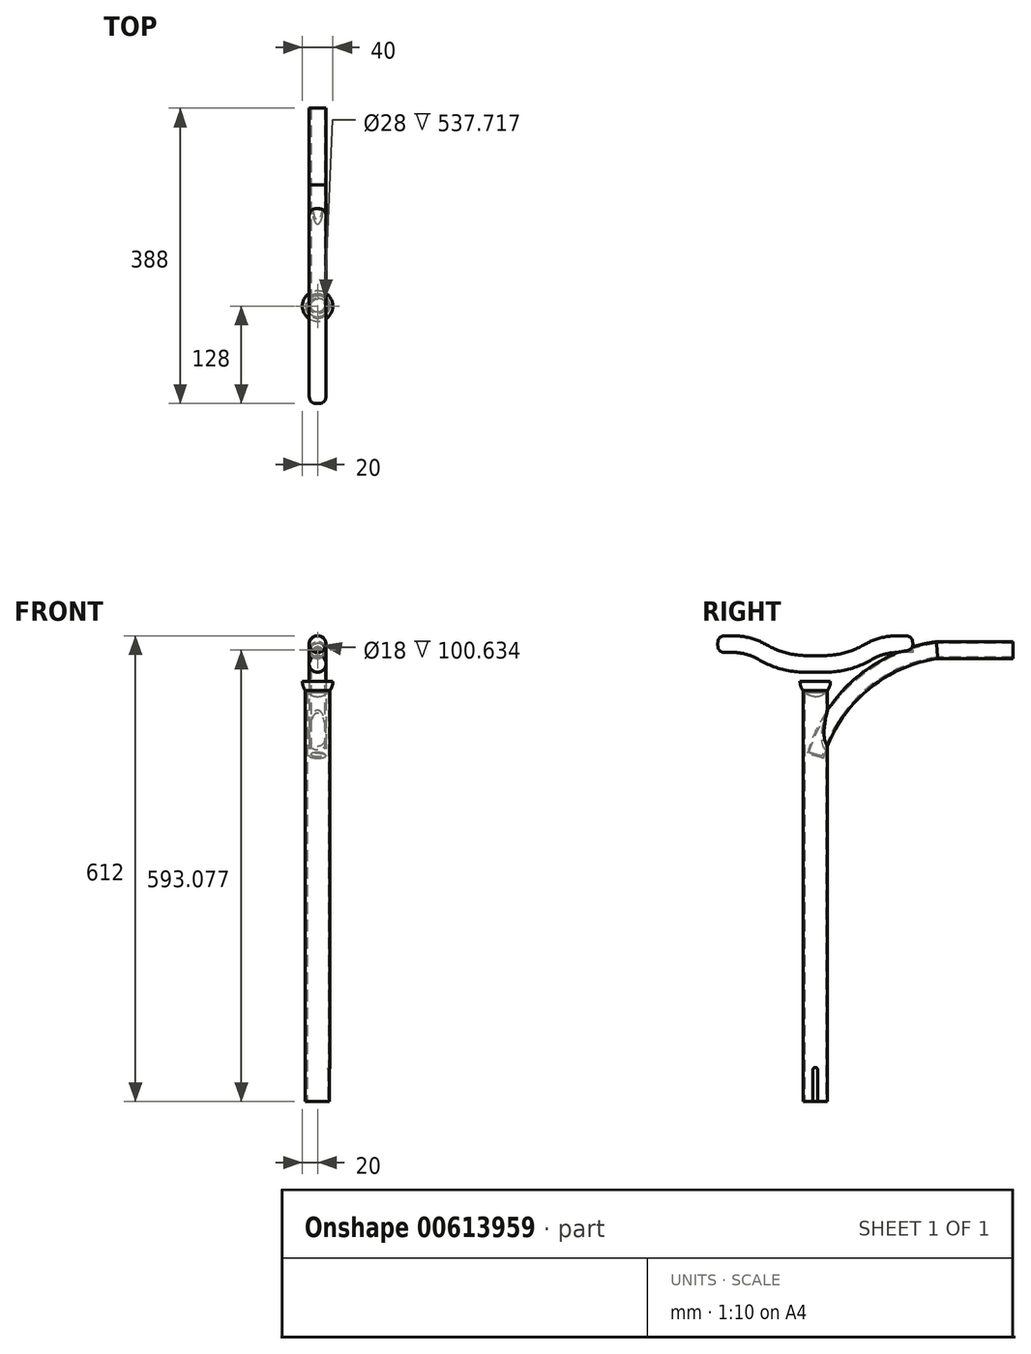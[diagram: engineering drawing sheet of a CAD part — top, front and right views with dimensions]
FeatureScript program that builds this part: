
annotation { "Feature Type Name" : "Feature", "Feature Type Description" : "" }
export const myFeature = defineFeature(function(context is Context, id is Id, definition is map)
    precondition{}
    {
        {
            var Q0;
            Q0=qCreatedBy(makeId("Top.planeOp"),FACE);
            var sketch = newSketch(context, id + "F0", { "sketchPlane" : qUnion([Q0])});
            skCircle(sketch, "E0", {"center": v(0, 0) * mm, "radius": 16 * mm});
            skSolve(sketch);
        }
        {
            var Q0;
            Q0 = qSketchRegion(id + "F0", true);
            extrude(context, id + "F1", {"entities" : qUnion([Q0]), "depth" : 550 * mm, "offsetDistance" : 25 * mm});
        }
        {
            var Q0;
            Q0=makeQuery(id+"F1.opExtrude","CAP_FACE",FACE,{"disambiguationData":[OSD([sQuery(id+"F0.wireOp",EDGE,"E0")])],"isStart":true});
            shell(context, id + "F2", {"entities" : qUnion([Q0]), "thickness" : 2 * mm});
        }
        {
            var Q0;
            Q0=qCreatedBy(makeId("Right.planeOp"),FACE);
            var sketch = newSketch(context, id + "F3", { "sketchPlane" : qUnion([Q0])});
            skLineSegment(sketch, "E1.bottom", {"start": v(-3, 0) * mm, "end": v(3, 0) * mm});
            skLineSegment(sketch, "E1.top", {"start": v(0, 45) * mm, "end": v(0, 45) * mm});
            skLineSegment(sketch, "E1.left", {"start": v(-3, 0) * mm, "end": v(-3, 42) * mm});
            skLineSegment(sketch, "E1.right", {"start": v(3, 0) * mm, "end": v(3, 42) * mm});
            skPoint(sketch, "E2.visualSharp", {"position": v(-3, 45) * mm});
            skArc(sketch, "E2.filletArc", {"start": v(0, 45) * mm, "mid": v(-2.12, 44.12) * mm, "end": v(-3, 42) * mm});
            skPoint(sketch, "E3.visualSharp", {"position": v(3, 45) * mm});
            skArc(sketch, "E3.filletArc", {"start": v(3, 42) * mm, "mid": v(2.12, 44.12) * mm, "end": v(0, 45) * mm});
            skSolve(sketch);
        }
        {
            var Q0;
            Q0 = qSketchRegion(id + "F3", true);
            extrude(context, id + "F4", {"entities" : qUnion([Q0]), "operationType" : NewBodyOperationType.REMOVE, "endBound" : BoundingType.THROUGH_ALL, "depth" : 25 * mm, "offsetDistance" : 25 * mm});
        }
        {
            var Q0;
            Q0=qCreatedBy(makeId("Right.planeOp"),FACE);
            var sketch = newSketch(context, id + "F5", { "sketchPlane" : qUnion([Q0])});
            skArc(sketch, "E4", {"start": v(160, 593.08) * mm, "mid": v(59.5, 547.27) * mm, "end": v(0, 454.2) * mm});
            skLineSegment(sketch, "E5", {"start": v(160, 593.08) * mm, "end": v(260, 593.08) * mm});
            skSolve(sketch);
        }
        {
            var Q0;
            Q0=sQuery(id+"F5.wireOp",VERTEX,"E5.end");
            var Q1;
            Q1=qCreatedBy(makeId("Front.planeOp"),FACE);
            cPlane(context, id + "F6", {"entities" : qUnion([Q0, Q1]), "cplaneType" : CPlaneType.PLANE_POINT, "offset" : 25 * mm, "width" : 150 * mm, "height" : 150 * mm});
        }
        {
            var Q0;
            Q0=qCreatedBy(id+"F6.planeOp",FACE);
            var sketch = newSketch(context, id + "F7", { "sketchPlane" : qUnion([Q0])});
            skCircle(sketch, "E6", {"center": v(0, 593.08) * mm, "radius": 11 * mm});
            skSolve(sketch);
        }
        {
            var Q0;
            Q0=makeQuery(id+"F7.imprint","IMPRINT",FACE,{"disambiguationData":[TD([[makeQuery(id+"F7.imprint","IMPRINT",EDGE,{"derivedFrom":sQuery(id+"F7.wireOp",EDGE,"E6")}),1.0]])]});
            var Q1;
            Q1=sQuery(id+"F5.wireOp",EDGE,"E4");
            var Q2;
            Q2=sQuery(id+"F5.wireOp",EDGE,"E5");
            sweep(context, id + "F8", {"operationType" : NewBodyOperationType.ADD, "profiles" : qUnion([Q0]), "path" : qUnion([Q1, Q2])});
        }
        {
            var Q0;
            Q0=makeQuery(id+"F8.opSweep","CAP_FACE",FACE,{"disambiguationData":[OSD([sQuery(id+"F5.wireOp",VERTEX,"E5.end"),sQuery(id+"F7.wireOp",EDGE,"E6")])],"isStart":true});
            shell(context, id + "F9", {"entities" : qUnion([Q0]), "thickness" : 2 * mm});
        }
        {
            var Q0;
            Q0=qCreatedBy(makeId("Right.planeOp"),FACE);
            var sketch = newSketch(context, id + "F10", { "sketchPlane" : qUnion([Q0])});
            skLineSegment(sketch, "E7", {"start": v(0, 356.72) * mm, "end": v(0, 575) * mm, "construction": true});
            skLineSegment(sketch, "E8", {"start": v(-128, 601) * mm, "end": v(-108, 601) * mm});
            skArc(sketch, "E9", {"start": v(-69.28, 590.46) * mm, "mid": v(-87.93, 598.32) * mm, "end": v(-108, 601) * mm});
            skLineSegment(sketch, "E10", {"start": v(0, 575) * mm, "end": v(-12.5, 575) * mm});
            skArc(sketch, "E11", {"start": v(-69.28, 590.46) * mm, "mid": v(-41.92, 578.93) * mm, "end": v(-12.5, 575) * mm});
            skLineSegment(sketch, "E12.MirrorCS", {"start": v(0, 575) * mm, "end": v(12.5, 575) * mm});
            skArc(sketch, "E13.MirrorCS", {"start": v(69.28, 590.46) * mm, "mid": v(41.92, 578.93) * mm, "end": v(12.5, 575) * mm});
            skArc(sketch, "E14.MirrorCS", {"start": v(69.28, 590.46) * mm, "mid": v(87.93, 598.32) * mm, "end": v(108, 601) * mm});
            skLineSegment(sketch, "E15.MirrorCS", {"start": v(128, 601) * mm, "end": v(108, 601) * mm});
            skSolve(sketch);
        }
        {
            var Q0;
            Q0=sQuery(id+"F10.wireOp",VERTEX,"E15.MirrorCS.start");
            var Q1;
            Q1=qCreatedBy(id+"F6.planeOp",FACE);
            cPlane(context, id + "F11", {"entities" : qUnion([Q0, Q1]), "cplaneType" : CPlaneType.PLANE_POINT, "offset" : 25 * mm, "width" : 150 * mm, "height" : 150 * mm});
        }
        {
            var Q0;
            Q0=qCreatedBy(id+"F11.planeOp",FACE);
            var sketch = newSketch(context, id + "F12", { "sketchPlane" : qUnion([Q0])});
            skCircle(sketch, "E16", {"center": v(0, 601) * mm, "radius": 11 * mm});
            skSolve(sketch);
        }
        {
            var Q0;
            Q0 = qSketchRegion(id + "F12", true);
            var Q1;
            Q1 = qConstructionFilter(qBodyType(qCreatedBy(id + "F10" ,EDGE), BodyType.WIRE), ConstructionObject.NO);
            sweep(context, id + "F13", {"operationType" : NewBodyOperationType.ADD, "profiles" : qUnion([Q0]), "path" : qUnion([Q1])});
        }
        {
            var Q0;
            Q0=makeQuery(id+"F13.opSweep","CAP_EDGE",EDGE,{"disambiguationData":[OSD([sQuery(id+"F10.wireOp",VERTEX,"E8.start"),sQuery(id+"F12.wireOp",EDGE,"E16")])],"isStart":false});
            var Q1;
            {var subQ0=sQuery(id+"F12.wireOp",EDGE,"E16");var subQ1=sQuery(id+"F10.wireOp",VERTEX,"E15.MirrorCS.start");Q1=makeQuery(id+"F13.boolean.opBoolean","SPLIT",EDGE,{"disambiguationData":[TD([makeQuery(id+"F8.opSweep","SWEPT_FACE",FACE,{"disambiguationData":[OSD([sQuery(id+"F5.wireOp",EDGE,"E4"),sQuery(id+"F7.wireOp",EDGE,"E6")])]})])],"derivedFrom":makeQuery(id+"F13.opSweep","CAP_EDGE",EDGE,{"disambiguationData":[OSD([subQ1,subQ0])],"isStart":true})});}
            fillet(context, id + "F14", {"entities" : qUnion([Q0, Q1]), "radius" : 10 * mm, "tangentPropagation" : true, "rho" : 0.5, "crossSection" : FilletCrossSection.CONIC, "allowEdgeOverflow" : false});
        }
        {
            var Q0;
            Q0=qCreatedBy(makeId("Right.planeOp"),FACE);
            var sketch = newSketch(context, id + "F15", { "sketchPlane" : qUnion([Q0])});
            skArc(sketch, "E17", {"start": v(-20, 552) * mm, "mid": v(-14.14, 537.86) * mm, "end": v(0, 532) * mm});
            skLineSegment(sketch, "E18", {"start": v(0, 552) * mm, "end": v(-20, 552) * mm});
            skLineSegment(sketch, "E19", {"start": v(-20, 552) * mm, "end": v(0, 552) * mm});
            skLineSegment(sketch, "E20", {"start": v(0, 552) * mm, "end": v(0, 532) * mm});
            skSolve(sketch);
        }
        {
            var Q0;
            Q0=makeQuery(id+"F15.imprint","IMPRINT",FACE,{"disambiguationData":[TD([[makeQuery(id+"F15.imprint","IMPRINT",EDGE,{"derivedFrom":sQuery(id+"F15.wireOp",EDGE,"E17")}),1.0]])]});
            var Q1;
            Q1=makeQuery(id+"F1.opExtrude","SWEPT_FACE",FACE,{"disambiguationData":[OSD([sQuery(id+"F0.wireOp",EDGE,"E0")])]});
            revolve(context, id + "F16", {"operationType" : NewBodyOperationType.ADD, "surfaceOperationType" : NewSurfaceOperationType.NEW, "entities" : qUnion([Q0]), "axis" : qUnion([Q1]), "revolveType" : RevolveType.FULL});
        }
    });
